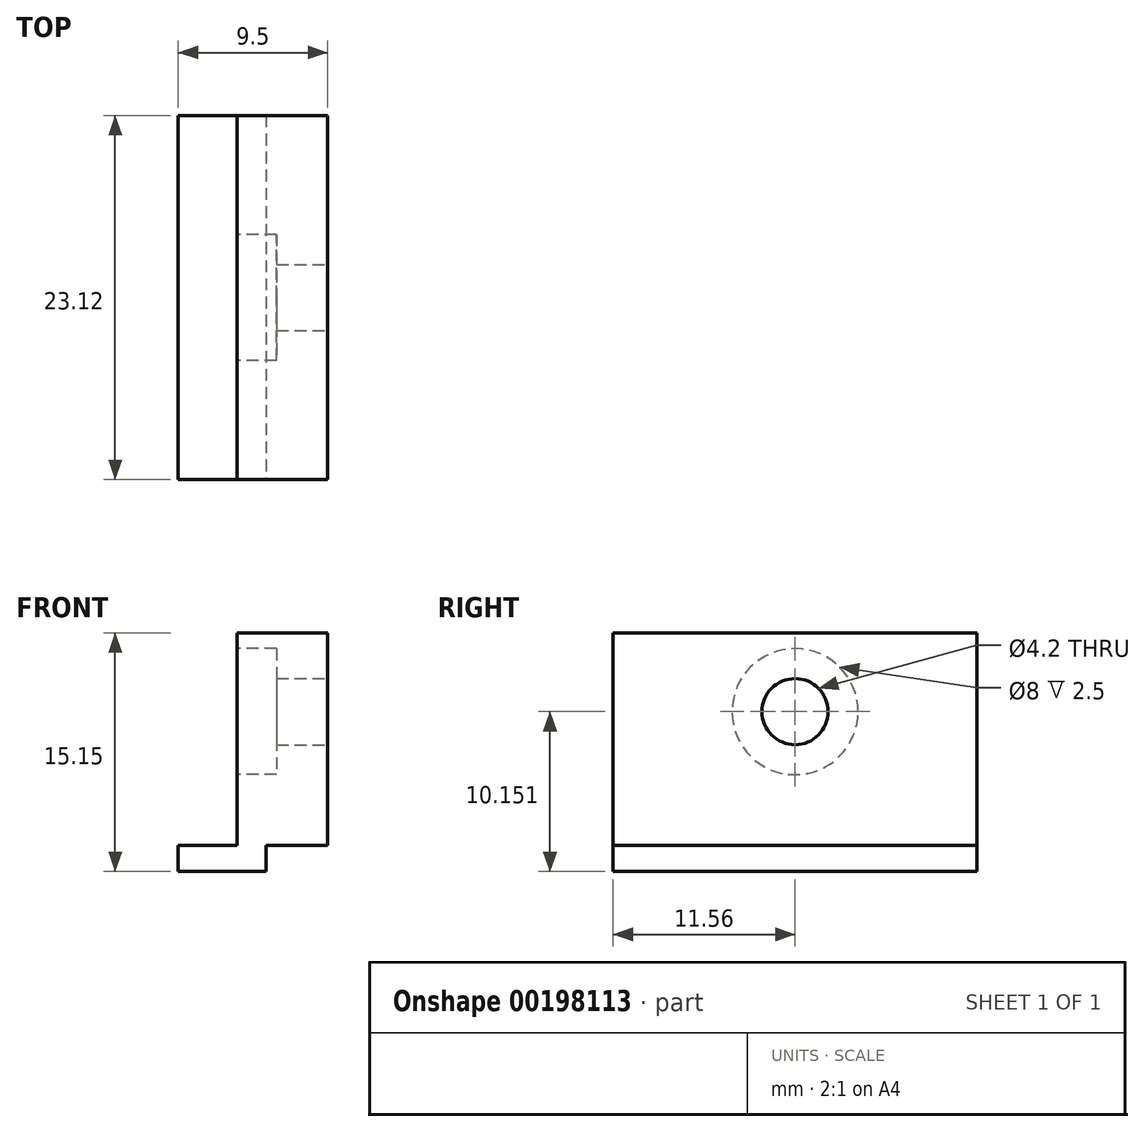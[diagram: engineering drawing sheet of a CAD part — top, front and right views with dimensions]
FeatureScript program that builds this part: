
annotation { "Feature Type Name" : "Feature", "Feature Type Description" : "" }
export const myFeature = defineFeature(function(context is Context, id is Id, definition is map)
    precondition{}
    {
        {
            var Q0;
            Q0=qCreatedBy(makeId("Top.planeOp"),FACE);
            var sketch = newSketch(context, id + "F0", { "sketchPlane" : qUnion([Q0])});
            skLineSegment(sketch, "E0.bottom", {"start": v(-2.8, 11.56) * mm, "end": v(2.8, 11.56) * mm});
            skLineSegment(sketch, "E0.top", {"start": v(-2.8, -11.56) * mm, "end": v(2.8, -11.56) * mm});
            skLineSegment(sketch, "E0.left", {"start": v(-2.8, 11.56) * mm, "end": v(-2.8, -11.56) * mm});
            skLineSegment(sketch, "E0.right", {"start": v(2.8, 11.56) * mm, "end": v(2.8, -11.56) * mm});
            skPoint(sketch, "E0.middle", {"position": v(0, 0) * mm});
            skSolve(sketch);
        }
        {
            var Q0;
            Q0 = qSketchRegion(id + "F0", true);
            extrude(context, id + "F1", {"entities" : qUnion([Q0]), "depth" : 1.65 * mm});
        }
        {
            var Q0;
            Q0=makeQuery(id+"F1.opExtrude","CAP_FACE",FACE,{"disambiguationData":[OSD([sQuery(id+"F0.wireOp",EDGE,"E0.bottom"),sQuery(id+"F0.wireOp",EDGE,"E0.top"),sQuery(id+"F0.wireOp",EDGE,"E0.left"),sQuery(id+"F0.wireOp",EDGE,"E0.right")])],"isStart":false});
            var sketch = newSketch(context, id + "F2", { "sketchPlane" : qUnion([Q0])});
            skLineSegment(sketch, "E1.bottom", {"start": v(0.96, 11.56) * mm, "end": v(6.7, 11.56) * mm});
            skLineSegment(sketch, "E1.top", {"start": v(0.96, -11.56) * mm, "end": v(6.7, -11.56) * mm});
            skLineSegment(sketch, "E1.left", {"start": v(0.96, 11.56) * mm, "end": v(0.96, -11.56) * mm});
            skLineSegment(sketch, "E1.right", {"start": v(6.7, 11.56) * mm, "end": v(6.7, -11.56) * mm});
            skSolve(sketch);
        }
        {
            var Q0;
            Q0 = qSketchRegion(id + "F2", true);
            extrude(context, id + "F3", {"entities" : qUnion([Q0]), "operationType" : NewBodyOperationType.ADD, "depth" : 13.5 * mm});
        }
        {
            var Q0;
            Q0=makeQuery(id+"F3.opExtrude","SWEPT_FACE",FACE,{"disambiguationData":[OSD([sQuery(id+"F2.wireOp",EDGE,"E1.right")])]});
            var sketch = newSketch(context, id + "F4", { "sketchPlane" : qUnion([Q0])});
            skCircle(sketch, "E2", {"center": v(0, 10.15) * mm, "radius": 2.1 * mm});
            skSolve(sketch);
        }
        {
            var Q0;
            Q0 = qSketchRegion(id + "F4", true);
            extrude(context, id + "F5", {"entities" : qUnion([Q0]), "operationType" : NewBodyOperationType.REMOVE, "oppositeDirection" : true, "depth" : 25.4 * mm});
        }
        {
            var Q0;
            Q0=makeQuery(id+"F3.opExtrude","SWEPT_FACE",FACE,{"disambiguationData":[OSD([sQuery(id+"F2.wireOp",EDGE,"E1.left")])]});
            var sketch = newSketch(context, id + "F6", { "sketchPlane" : qUnion([Q0])});
            skCircle(sketch, "E3", {"center": v(0, 10.15) * mm, "radius": 4 * mm});
            skSolve(sketch);
        }
        {
            var Q0;
            Q0 = qSketchRegion(id + "F6", true);
            extrude(context, id + "F7", {"entities" : qUnion([Q0]), "operationType" : NewBodyOperationType.REMOVE, "oppositeDirection" : true, "depth" : 2.5 * mm});
        }
    });
